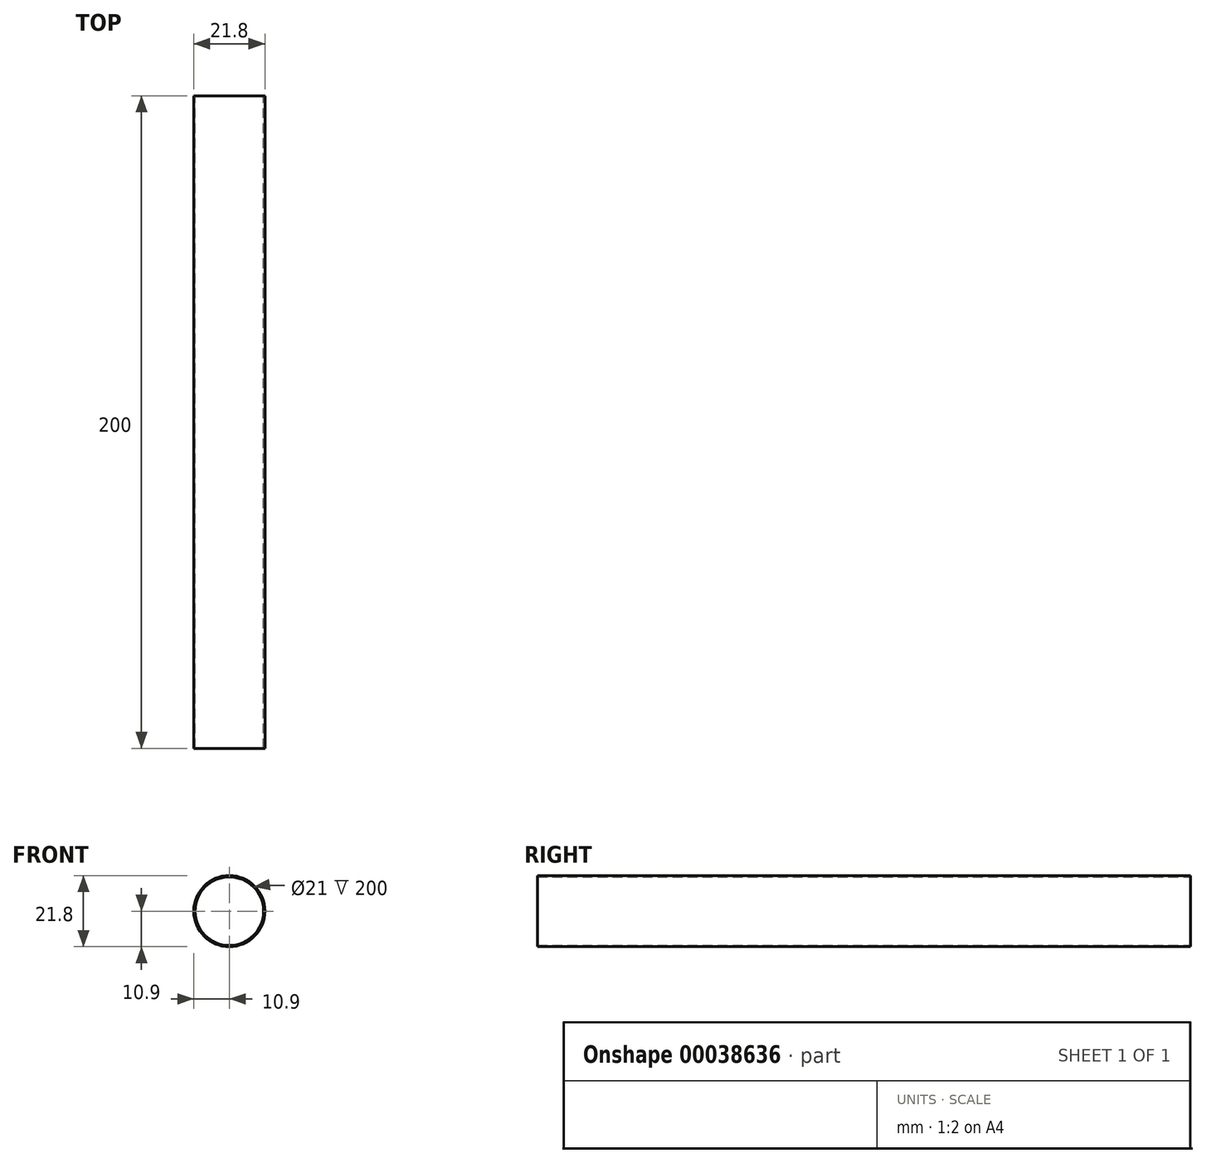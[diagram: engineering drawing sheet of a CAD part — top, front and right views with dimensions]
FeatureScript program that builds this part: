
annotation { "Feature Type Name" : "Feature", "Feature Type Description" : "" }
export const myFeature = defineFeature(function(context is Context, id is Id, definition is map)
    precondition{}
    {
        {
            var Q0;
            Q0=qCreatedBy(makeId("Front.planeOp"),FACE);
            var sketch = newSketch(context, id + "F0", { "sketchPlane" : qUnion([Q0])});
            skCircle(sketch, "E0", {"center": v(0, 0) * mm, "radius": 10.5 * mm});
            skCircle(sketch, "E1", {"center": v(0, 0) * mm, "radius": 10.9 * mm});
            skSolve(sketch);
        }
        {
            var Q0;
            Q0=makeQuery(id+"F0.imprint","IMPRINT",FACE,{"disambiguationData":[TD([[makeQuery(id+"F0.imprint","IMPRINT",EDGE,{"derivedFrom":sQuery(id+"F0.wireOp",EDGE,"E0")}),-1.0]])]});
            extrude(context, id + "F1", {"entities" : qUnion([Q0]), "depth" : 200 * mm});
        }
    });
